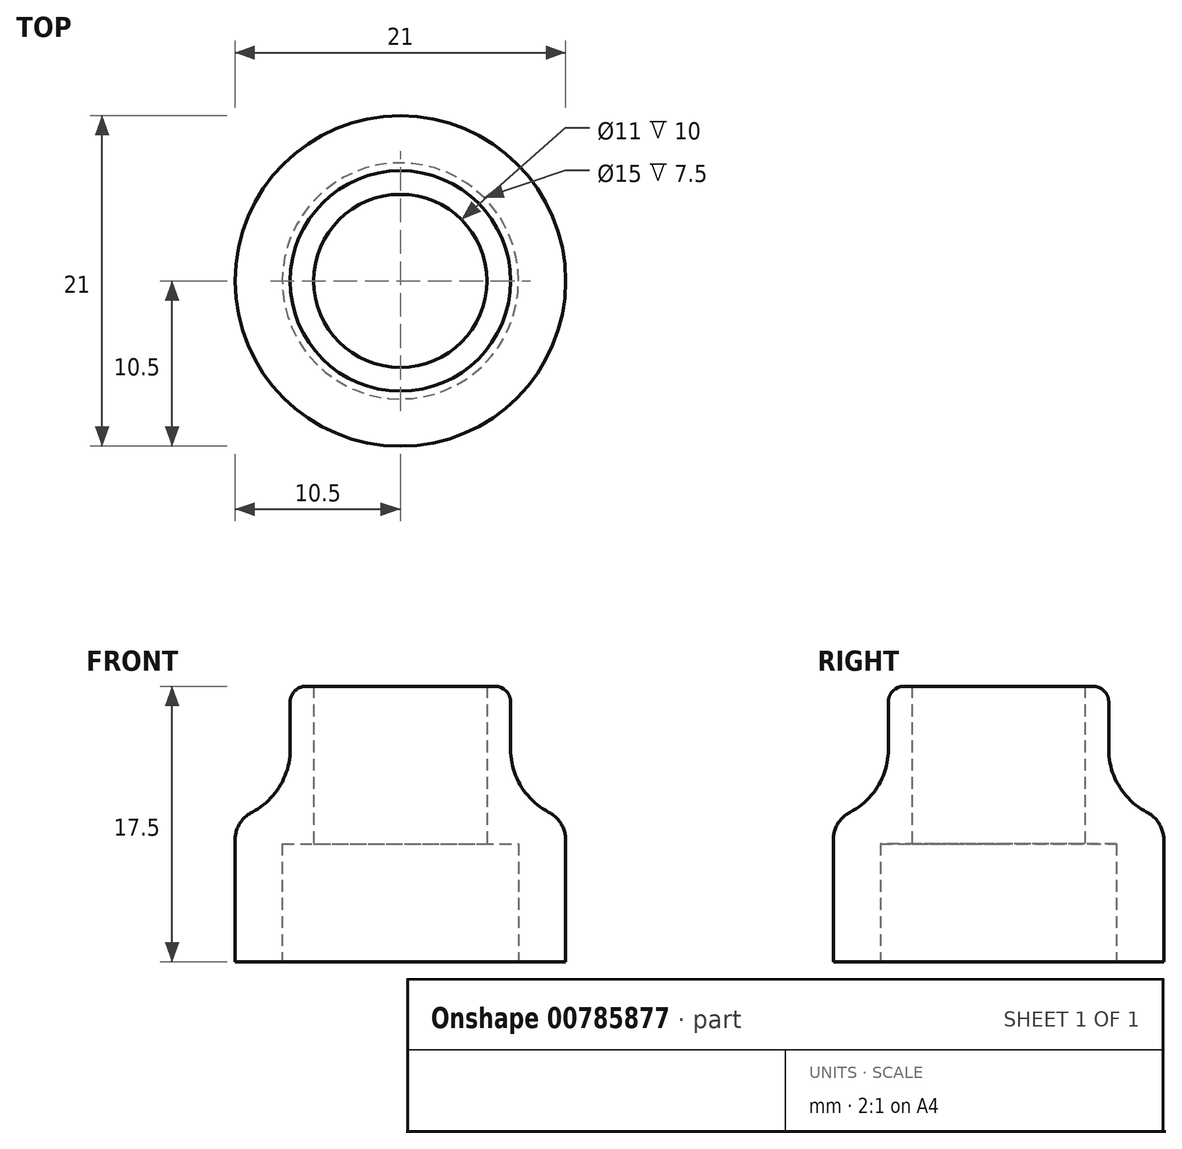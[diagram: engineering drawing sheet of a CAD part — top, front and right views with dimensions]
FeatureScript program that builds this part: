
annotation { "Feature Type Name" : "Feature", "Feature Type Description" : "" }
export const myFeature = defineFeature(function(context is Context, id is Id, definition is map)
    precondition{}
    {
        {
            var Q0;
            Q0=qCreatedBy(makeId("Front.planeOp"),FACE);
            var sketch = newSketch(context, id + "F0", { "sketchPlane" : qUnion([Q0])});
            skLineSegment(sketch, "E0", {"start": v(7.5, 0) * mm, "end": v(10.5, 0) * mm});
            skLineSegment(sketch, "E1", {"start": v(10.5, 0) * mm, "end": v(10.5, 7.73) * mm});
            skLineSegment(sketch, "E2", {"start": v(7, 13.5) * mm, "end": v(7, 16.5) * mm});
            skLineSegment(sketch, "E3", {"start": v(7.5, 7.5) * mm, "end": v(7.5, 0) * mm});
            skLineSegment(sketch, "E4", {"start": v(0, 0) * mm, "end": v(0, 18.32) * mm, "construction": true});
            skPoint(sketch, "E5.visualSharp", {"position": v(7, 9.03) * mm});
            skArc(sketch, "E6", {"start": v(9.42, 9.5) * mm, "mid": v(7.65, 11.17) * mm, "end": v(7, 13.5) * mm});
            skLineSegment(sketch, "E7", {"start": v(7, 13.5) * mm, "end": v(11.5, 13.5) * mm, "construction": true});
            skPoint(sketch, "E8.visualSharp", {"position": v(7, 17.5) * mm});
            skArc(sketch, "E8.filletArc", {"start": v(7, 16.5) * mm, "mid": v(6.7, 17.2) * mm, "end": v(6, 17.5) * mm});
            skPoint(sketch, "E9.visualSharp", {"position": v(10.5, 9.11) * mm});
            skArc(sketch, "E9.filletArc", {"start": v(10.5, 7.73) * mm, "mid": v(10.2, 8.77) * mm, "end": v(9.42, 9.5) * mm});
            skLineSegment(sketch, "E10", {"start": v(6, 17.5) * mm, "end": v(5.5, 17.5) * mm});
            skLineSegment(sketch, "E11", {"start": v(5.5, 17.5) * mm, "end": v(5.5, 7.5) * mm});
            skLineSegment(sketch, "E12", {"start": v(5.5, 7.5) * mm, "end": v(7.5, 7.5) * mm});
            skSolve(sketch);
        }
        {
            var Q0;
            Q0=makeQuery(id+"F0.imprint","IMPRINT",FACE,{"disambiguationData":[TD([[makeQuery(id+"F0.imprint","IMPRINT",EDGE,{"derivedFrom":sQuery(id+"F0.wireOp",EDGE,"E0")}),1.0]])]});
            var Q1;
            Q1=sQuery(id+"F0.wireOp",EDGE,"E4");
            revolve(context, id + "F1", {"surfaceOperationType" : NewSurfaceOperationType.NEW, "entities" : qUnion([Q0]), "axis" : qUnion([Q1]), "revolveType" : RevolveType.FULL});
        }
    });
